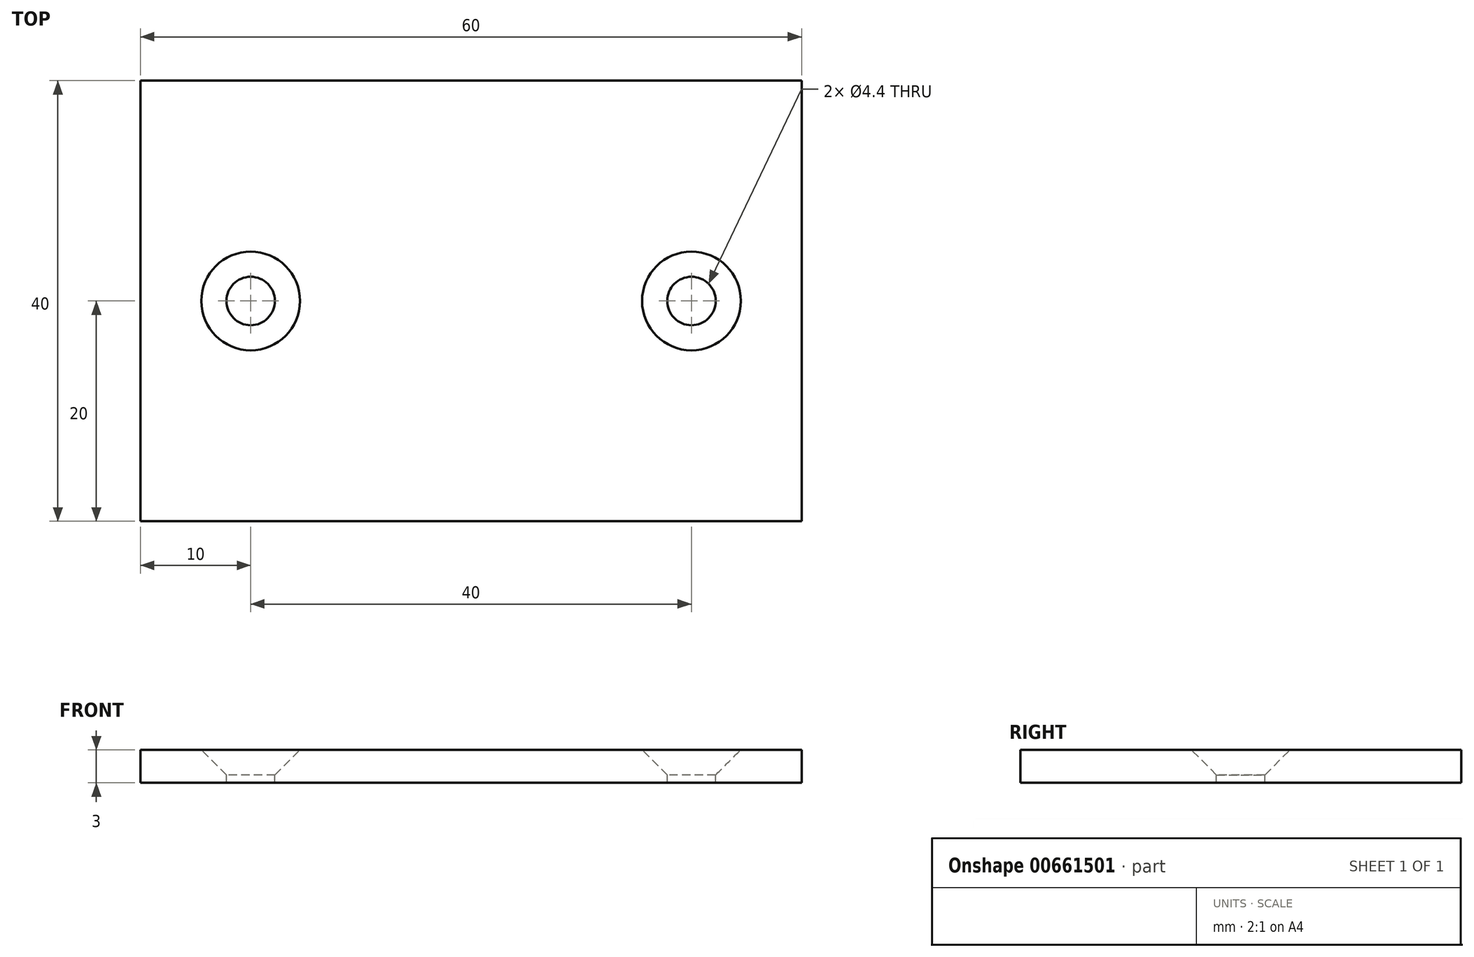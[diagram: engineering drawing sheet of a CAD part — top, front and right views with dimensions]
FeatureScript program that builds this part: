
annotation { "Feature Type Name" : "Feature", "Feature Type Description" : "" }
export const myFeature = defineFeature(function(context is Context, id is Id, definition is map)
    precondition{}
    {
        {
            var Q0;
            Q0=qCreatedBy(makeId("Top.planeOp"),FACE);
            var sketch = newSketch(context, id + "F0", { "sketchPlane" : qUnion([Q0])});
            skLineSegment(sketch, "E0.bottom", {"start": v(-30, -20) * mm, "end": v(30, -20) * mm});
            skLineSegment(sketch, "E0.top", {"start": v(-30, 20) * mm, "end": v(30, 20) * mm});
            skLineSegment(sketch, "E0.left", {"start": v(-30, -20) * mm, "end": v(-30, 20) * mm});
            skLineSegment(sketch, "E0.right", {"start": v(30, -20) * mm, "end": v(30, 20) * mm});
            skPoint(sketch, "E0.middle", {"position": v(0, 0) * mm});
            skSolve(sketch);
        }
        {
            var Q0;
            Q0 = qSketchRegion(id + "F0", true);
            extrude(context, id + "F1", {"entities" : qUnion([Q0]), "depth" : 3 * mm, "offsetDistance" : 25 * mm});
        }
        {
            var Q0;
            Q0=makeQuery(id+"F1.opExtrude","CAP_FACE",FACE,{"disambiguationData":[OSD([sQuery(id+"F0.wireOp",EDGE,"E0.bottom"),sQuery(id+"F0.wireOp",EDGE,"E0.top"),sQuery(id+"F0.wireOp",EDGE,"E0.left"),sQuery(id+"F0.wireOp",EDGE,"E0.right")])],"isStart":false});
            var sketch = newSketch(context, id + "F2", { "sketchPlane" : qUnion([Q0])});
            skPoint(sketch, "E1", {"position": v(-20, 0) * mm});
            skPoint(sketch, "E2", {"position": v(20, 0) * mm});
            skSolve(sketch);
        }
        {
            var Q0;
            Q0=sQuery(id+"F2.wireOp",VERTEX,"E1");
            var Q1;
            Q1=sQuery(id+"F2.wireOp",VERTEX,"E2");
            var Q2;
            Q2=makeQuery(id+"F1.opExtrude","SWEPT_BODY",BODY,{"disambiguationData":[OSD([sQuery(id+"F0.wireOp",EDGE,"E0.bottom"),sQuery(id+"F0.wireOp",EDGE,"E0.top"),sQuery(id+"F0.wireOp",EDGE,"E0.left"),sQuery(id+"F0.wireOp",EDGE,"E0.right")])]});
            hole(context, id + "F3", {"style" : HoleStyle.C_SINK, "endStyle" : HoleEndStyle.THROUGH, "standardTappedOrClearance" : lookupTablePath({ "standard" : "ISO", "fit" : "Normal", "size" : "M4", "type" : "Clearance" }), "standardBlindInLast" : lookupTablePath({ "fit" : "Standard", "standard" : "ISO", "size" : "M4", "type" : "Clearance" }), "holeDiameter" : 4.4 * mm, "cSinkDiameter" : 8.96 * mm, "cSinkAngle" : 90 * degree, "majorDiameter" : 5 * mm, "isTappedThrough" : true, "tappedDepth" : 12 * mm, "tapClearance" : 3, "startFromSketch" : true, "locations" : qUnion([Q0, Q1]), "scope" : qUnion([Q2])});
        }
    });
